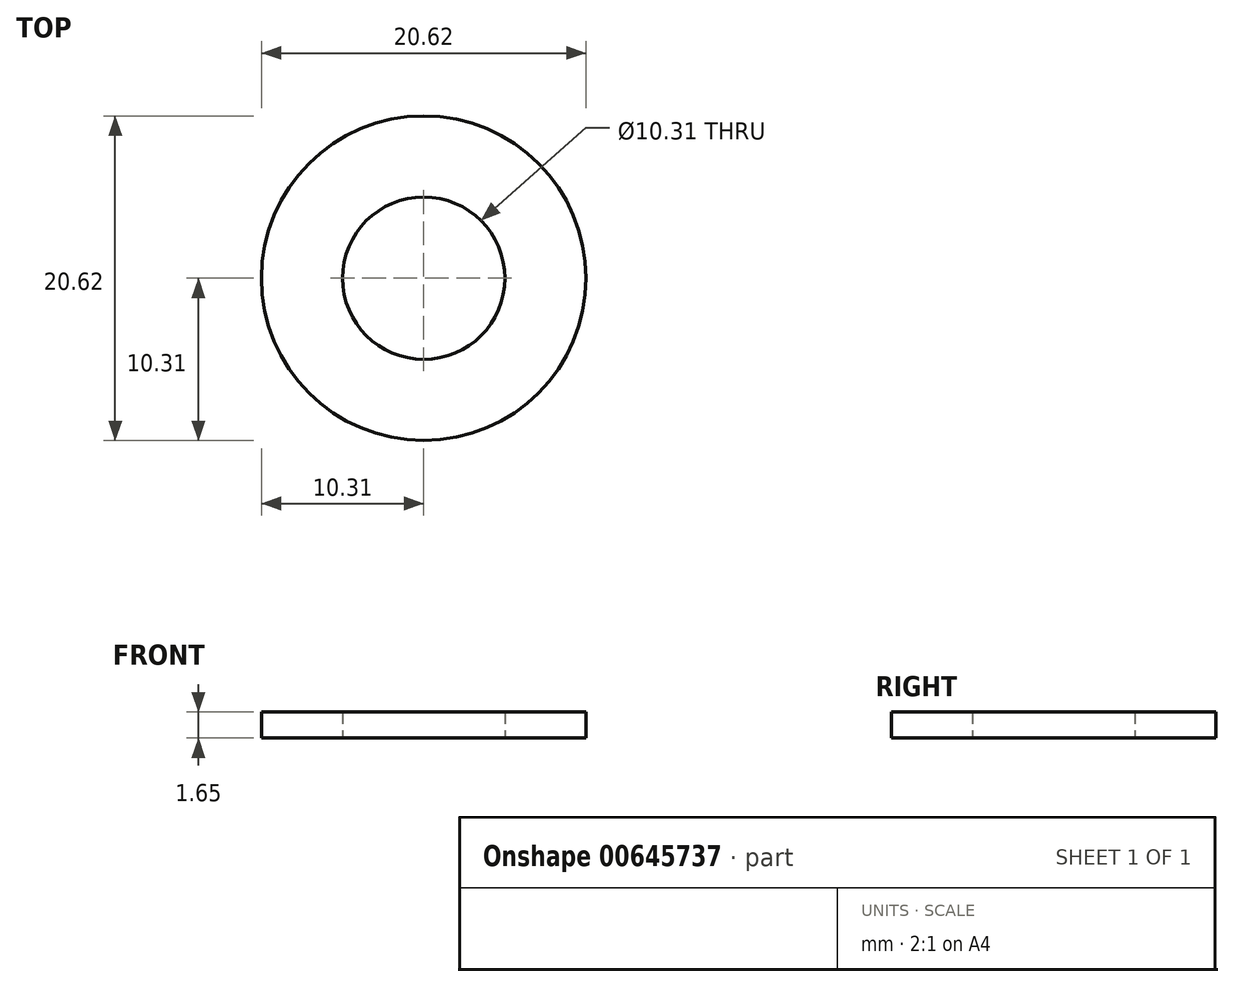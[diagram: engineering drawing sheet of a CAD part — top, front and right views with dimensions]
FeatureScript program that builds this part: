
annotation { "Feature Type Name" : "Feature", "Feature Type Description" : "" }
export const myFeature = defineFeature(function(context is Context, id is Id, definition is map)
    precondition{}
    {
        {
            var Q0;
            Q0=qCreatedBy(makeId("Top.planeOp"),FACE);
            var sketch = newSketch(context, id + "F0", { "sketchPlane" : qUnion([Q0])});
            skCircle(sketch, "E0", {"center": v(0, 0) * mm, "radius": 10.3 * mm});
            skCircle(sketch, "E1", {"center": v(0, 0) * mm, "radius": 5.16 * mm});
            skSolve(sketch);
        }
        {
            var Q0;
            Q0=makeQuery(id+"F0.imprint","IMPRINT",FACE,{"disambiguationData":[TD([[makeQuery(id+"F0.imprint","IMPRINT",EDGE,{"derivedFrom":sQuery(id+"F0.wireOp",EDGE,"E0")}),1.0]])]});
            extrude(context, id + "F1", {"entities" : qUnion([Q0]), "depth" : 1.65 * mm, "offsetDistance" : 25 * mm});
        }
    });
